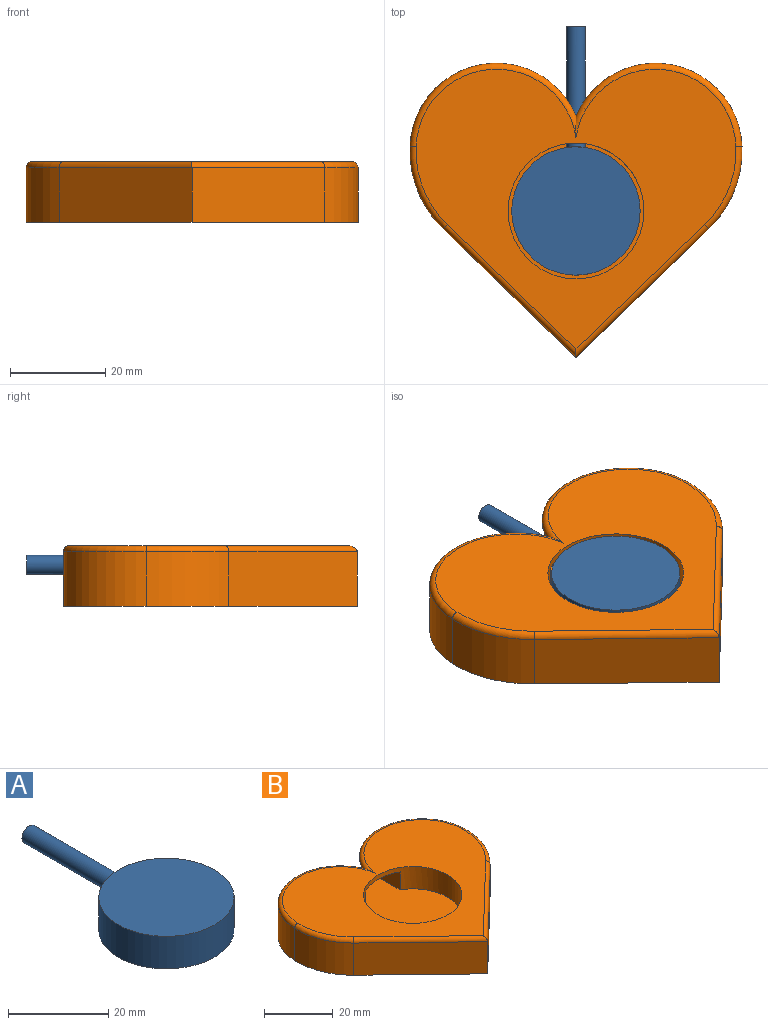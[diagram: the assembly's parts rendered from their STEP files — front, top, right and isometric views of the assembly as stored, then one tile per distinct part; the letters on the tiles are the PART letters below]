
ASSEMBLY  parts=2 mates=1
PART A: 5 faces, bbox 27x52.3x7.9 mm
  f0: cylinder r=13.49mm len=26.99mm, axis (0,0,1), area 660.5mm2, adj f1,f2,f3
  f1: plane 26.99x26.99mm, normal (0,0,-1), area 572mm2, adj f0
  f2: plane 26.99x26.99mm, normal (0,0,1), area 572mm2, adj f0
  f3: cylinder r=1.98mm len=25.41mm, axis (0,-1,0), area 315.9mm2, adj f0,f4
  f4: plane 3.97x3.97mm, normal (0,1,0), area 12.4mm2, adj f3
PART B: 19 faces, bbox 73.7x63.4x12.7 mm
  f0: cylinder r=18.2mm len=34.93mm, axis (0,0,1), area 490.2mm2, adj f1,f5,f6,f9,f10,f12,f18
  f1: cylinder r=18.2mm len=34.93mm, axis (0,0,1), area 490.2mm2, adj f0,f2,f6,f9,f10,f11,f16
  f2: cylinder r=22.89mm len=17.43mm, axis (0,0,1), area 221.1mm2, adj f1,f3,f6,f14
  f3: plane 27.95x26.98mm, normal (-0.69,-0.72,0), area 444.1mm2, adj f2,f4,f6,f13
  f4: plane 27.95x26.98mm, normal (0.69,-0.72,0), area 444.1mm2, adj f3,f5,f6,f15
  f5: cylinder r=22.89mm len=17.43mm, axis (0,0,1), area 221.1mm2, adj f0,f4,f6,f17
  f6: plane 69.89x61.85mm, normal (0,0,-1), area 2874.5mm2, adj f0,f1,f2,f3,f4,f5
  f7: plane 67.35x58.82mm, normal (0,0,1), area 1963.4mm2, adj f8,f13,f14,f15,f16,f17,f18
  f8: cylinder r=14.29mm len=28.58mm, axis (0,0,1), area 617.5mm2, adj f7,f9,f10,f11,f12
  f9: plane 42.65x28.58mm, normal (0,0,1), area 804.3mm2, adj f0,f1,f8,f11,f12
  f10: plane 15.99x14.29mm, normal (0,0,-1), area 163mm2, adj f0,f1,f8,f11,f12
  f11: plane 15.99x6.35mm, normal (1,0,0), area 101.6mm2, adj f1,f8,f9,f10
  f12: plane 15.99x6.35mm, normal (-1,0,0), area 101.6mm2, adj f0,f8,f9,f10
  f13: cylinder r=1.27mm len=28.83mm, axis (0.72,-0.69,0), area 76.6mm2, adj f3,f7,f14,f15
  f14: torus R=21.62mm, axis (0,0,1), area 37.8mm2, adj f2,f7,f13,f16
  f15: cylinder r=1.27mm len=28.83mm, axis (0.72,0.69,0), area 76.6mm2, adj f4,f7,f13,f17
  f16: torus R=16.93mm, axis (0,0,1), area 98mm2, adj f1,f7,f14,f18
  f17: torus R=21.62mm, axis (0,0,1), area 37.8mm2, adj f5,f7,f15,f18
  f18: torus R=16.93mm, axis (0,0,1), area 98mm2, adj f0,f7,f16,f17
PLACE A t=(0,-4.06,-3.97)mm
PLACE B at identity fixed
MATE revolute A.f0 <-> B.f8  axis (0,0,-1) through (0,-4.06,-7.94)mm
